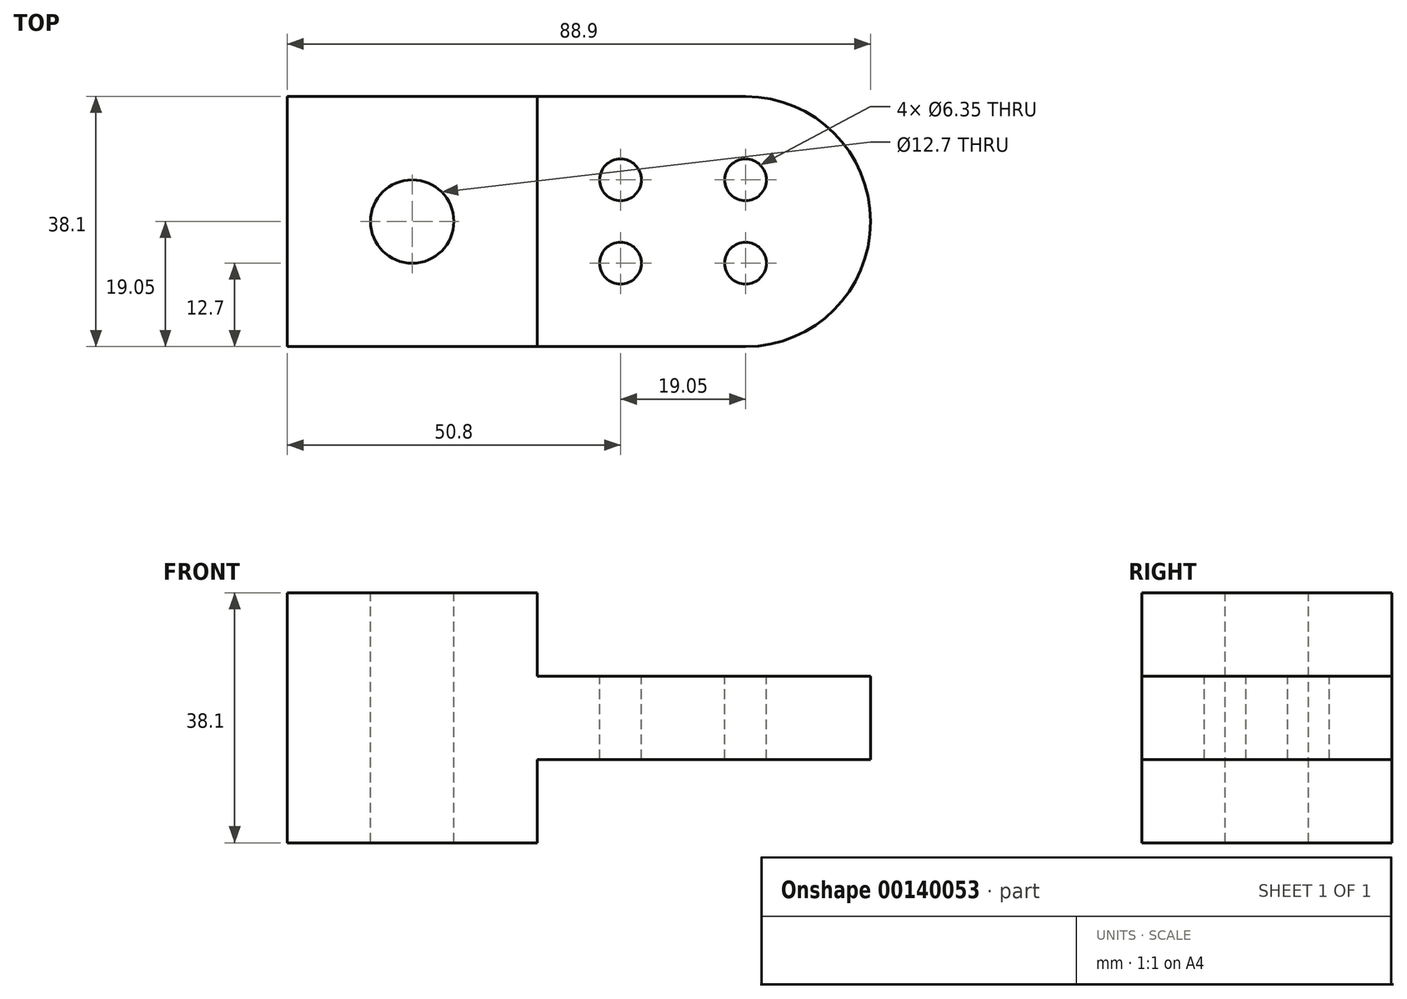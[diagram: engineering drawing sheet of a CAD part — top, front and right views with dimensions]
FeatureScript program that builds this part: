
annotation { "Feature Type Name" : "Feature", "Feature Type Description" : "" }
export const myFeature = defineFeature(function(context is Context, id is Id, definition is map)
    precondition{}
    {
        {
            var Q0;
            Q0=qCreatedBy(makeId("Front.planeOp"),FACE);
            var sketch = newSketch(context, id + "F0", { "sketchPlane" : qUnion([Q0])});
            skLineSegment(sketch, "E0", {"start": v(0, 0) * mm, "end": v(0, 38.1) * mm});
            skLineSegment(sketch, "E1", {"start": v(0, 38.1) * mm, "end": v(38.1, 38.1) * mm});
            skLineSegment(sketch, "E2", {"start": v(38.1, 38.1) * mm, "end": v(38.1, 25.4) * mm});
            skLineSegment(sketch, "E3", {"start": v(38.1, 25.4) * mm, "end": v(88.9, 25.4) * mm});
            skLineSegment(sketch, "E4", {"start": v(88.9, 25.4) * mm, "end": v(88.9, 12.7) * mm});
            skLineSegment(sketch, "E5", {"start": v(88.9, 12.7) * mm, "end": v(38.1, 12.7) * mm});
            skLineSegment(sketch, "E6", {"start": v(38.1, 12.7) * mm, "end": v(38.1, 0) * mm});
            skLineSegment(sketch, "E7", {"start": v(38.1, 0) * mm, "end": v(0, 0) * mm});
            skSolve(sketch);
        }
        {
            var Q0;
            Q0 = qSketchRegion(id + "F0", true);
            extrude(context, id + "F1", {"entities" : qUnion([Q0]), "depth" : 38.1 * mm});
        }
        {
            var Q0;
            Q0=makeQuery(id+"F1.opExtrude","SWEPT_FACE",FACE,{"disambiguationData":[OSD([sQuery(id+"F0.wireOp",EDGE,"E3")])]});
            var sketch = newSketch(context, id + "F2", { "sketchPlane" : qUnion([Q0])});
            skLineSegment(sketch, "E8", {"start": v(69.85, 0) * mm, "end": v(69.85, -38.1) * mm, "construction": true});
            skArc(sketch, "E9", {"start": v(69.85, -38.1) * mm, "mid": v(88.9, -19.05) * mm, "end": v(69.85, 0) * mm});
            skSolve(sketch);
        }
        {
            var Q0;
            Q0 = qSketchRegion(id + "F2", true);
            var Q1;
            {var subQ0=sQuery(id+"F2.wireOp",EDGE,"E9");var subQ1=sQuery(id+"F0.wireOp",EDGE,"E3");var subQ2=makeQuery(id+"F1.opExtrude","CAP_EDGE",EDGE,{"disambiguationData":[OSD([subQ1])],"isStart":false});var subQ3=makeQuery(id+"F2.imprint","INTERSECT",VERTEX,{"derivedFrom":[subQ2,subQ0]});Q1=makeQuery(id+"F2.imprint","IMPRINT",FACE,{"disambiguationData":[TD([[makeQuery(id+"F2.imprint","IMPRINT",EDGE,{"disambiguationData":[TD([[subQ3,-1.0]])],"derivedFrom":subQ0}),-1.0]])]});}
            var Q2;
            {var subQ0=sQuery(id+"F2.wireOp",EDGE,"E9");var subQ1=sQuery(id+"F0.wireOp",EDGE,"E3");var subQ2=makeQuery(id+"F1.opExtrude","CAP_EDGE",EDGE,{"disambiguationData":[OSD([subQ1])],"isStart":true});var subQ3=makeQuery(id+"F2.imprint","INTERSECT",VERTEX,{"derivedFrom":[subQ2,subQ0]});Q2=makeQuery(id+"F2.imprint","IMPRINT",FACE,{"disambiguationData":[TD([[makeQuery(id+"F2.imprint","IMPRINT",EDGE,{"disambiguationData":[TD([[subQ3,1.0]])],"derivedFrom":subQ0}),-1.0]])]});}
            extrude(context, id + "F3", {"entities" : qUnion([Q0, Q1, Q2]), "operationType" : NewBodyOperationType.REMOVE, "oppositeDirection" : true, "depth" : 12.7 * mm});
        }
        {
            var Q0;
            Q0=makeQuery(id+"F1.opExtrude","SWEPT_FACE",FACE,{"disambiguationData":[OSD([sQuery(id+"F0.wireOp",EDGE,"E3")])]});
            var sketch = newSketch(context, id + "F4", { "sketchPlane" : qUnion([Q0])});
            skLineSegment(sketch, "E10", {"start": v(50.8, -38.1) * mm, "end": v(50.8, 0) * mm, "construction": true});
            skLineSegment(sketch, "E11", {"start": v(69.85, 0) * mm, "end": v(69.85, -38.1) * mm, "construction": true});
            skCircle(sketch, "E12", {"center": v(50.8, -25.4) * mm, "radius": 3.18 * mm});
            skCircle(sketch, "E13", {"center": v(50.8, -12.7) * mm, "radius": 3.18 * mm});
            skCircle(sketch, "E14", {"center": v(69.85, -25.4) * mm, "radius": 3.18 * mm});
            skCircle(sketch, "E15", {"center": v(69.85, -12.7) * mm, "radius": 3.18 * mm});
            skSolve(sketch);
        }
        {
            var Q0;
            Q0 = qSketchRegion(id + "F4", true);
            extrude(context, id + "F5", {"entities" : qUnion([Q0]), "operationType" : NewBodyOperationType.REMOVE, "oppositeDirection" : true, "depth" : 12.7 * mm});
        }
        {
            var Q0;
            Q0=makeQuery(id+"F1.opExtrude","SWEPT_FACE",FACE,{"disambiguationData":[OSD([sQuery(id+"F0.wireOp",EDGE,"E1")])]});
            var sketch = newSketch(context, id + "F6", { "sketchPlane" : qUnion([Q0])});
            skCircle(sketch, "E16", {"center": v(19.05, -19.05) * mm, "radius": 6.35 * mm});
            skPoint(sketch, "E16.centerSnap0", {"position": v(19.05, 0) * mm});
            skPoint(sketch, "E16.centerSnap1", {"position": v(38.1, -19.05) * mm});
            skSolve(sketch);
        }
        {
            var Q0;
            Q0 = qSketchRegion(id + "F6", true);
            extrude(context, id + "F7", {"entities" : qUnion([Q0]), "operationType" : NewBodyOperationType.REMOVE, "oppositeDirection" : true, "depth" : 38.1 * mm});
        }
    });
